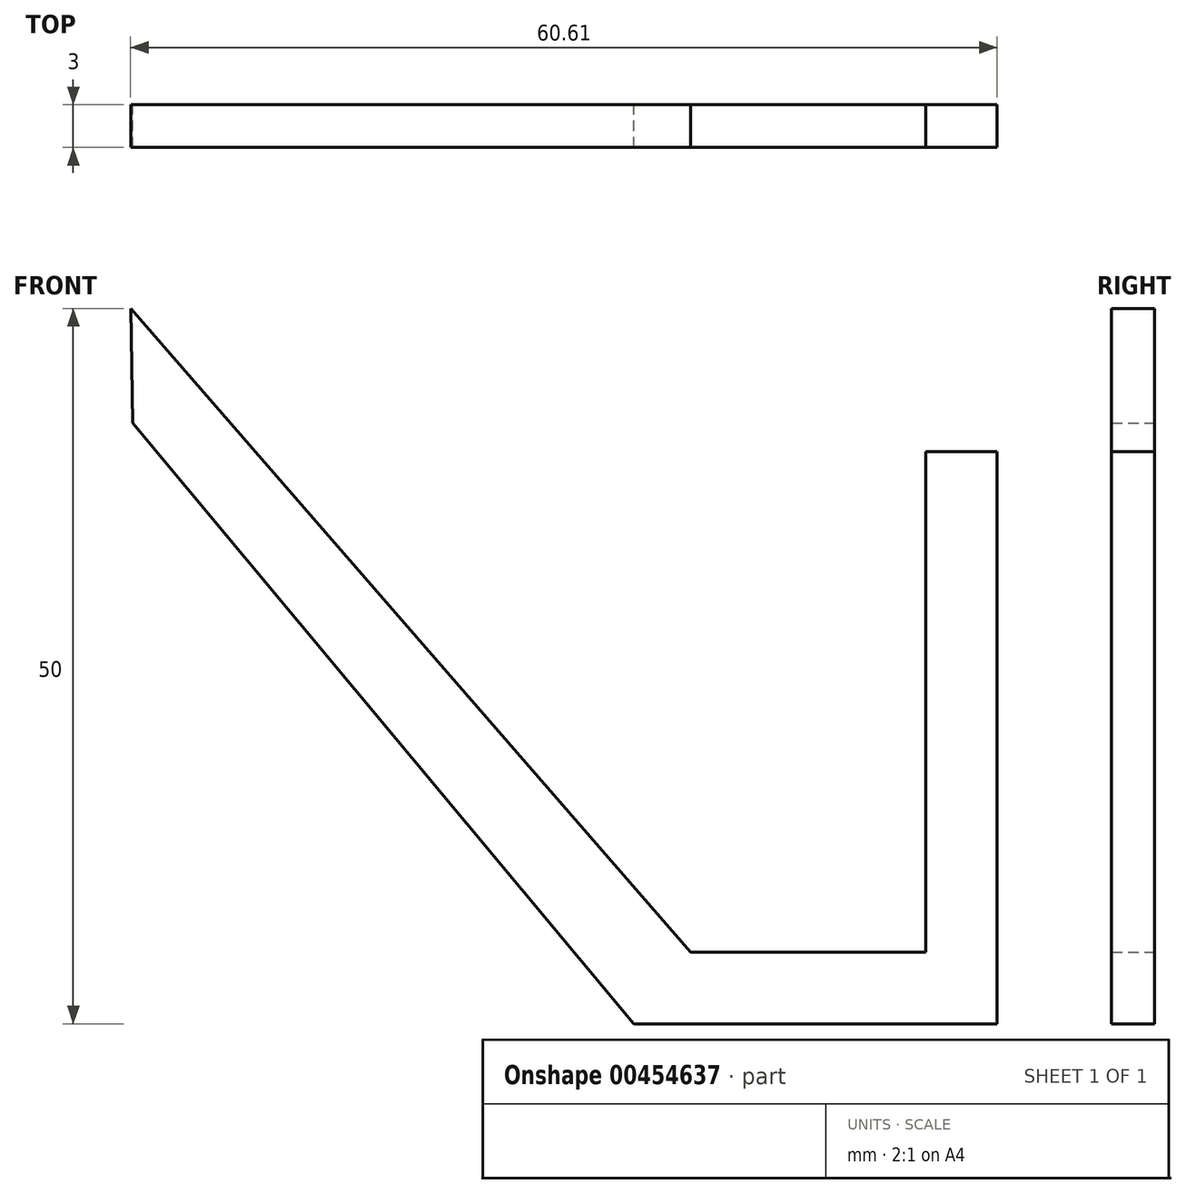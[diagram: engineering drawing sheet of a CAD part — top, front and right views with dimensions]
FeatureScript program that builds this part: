
annotation { "Feature Type Name" : "Feature", "Feature Type Description" : "" }
export const myFeature = defineFeature(function(context is Context, id is Id, definition is map)
    precondition{}
    {
        {
            var Q0;
            Q0=qCreatedBy(makeId("Front.planeOp"),FACE);
            var sketch = newSketch(context, id + "F0", { "sketchPlane" : qUnion([Q0])});
            skLineSegment(sketch, "E0", {"start": v(0, 0) * mm, "end": v(25.4, 0) * mm});
            skLineSegment(sketch, "E1", {"start": v(25.4, 0) * mm, "end": v(25.4, 5) * mm});
            skLineSegment(sketch, "E2", {"start": v(20.4, 5) * mm, "end": v(3.96, 5) * mm});
            skLineSegment(sketch, "E3", {"start": v(3.96, 5) * mm, "end": v(-35.2, 50) * mm});
            skLineSegment(sketch, "E4", {"start": v(0, 0) * mm, "end": v(-35.06, 42) * mm});
            skLineSegment(sketch, "E5", {"start": v(-35.06, 42) * mm, "end": v(-35.2, 50) * mm});
            skLineSegment(sketch, "E6.bottom", {"start": v(25.4, 0) * mm, "end": v(20.4, 0) * mm});
            skLineSegment(sketch, "E6.top", {"start": v(25.4, 40) * mm, "end": v(20.4, 40) * mm});
            skLineSegment(sketch, "E6.left", {"start": v(25.4, 0) * mm, "end": v(25.4, 40) * mm});
            skLineSegment(sketch, "E6.right", {"start": v(20.4, 5) * mm, "end": v(20.4, 40) * mm});
            skSolve(sketch);
        }
        {
            var Q0;
            Q0 = qSketchRegion(id + "F0", true);
            extrude(context, id + "F1", {"entities" : qUnion([Q0]), "depth" : 3 * mm});
        }
    });
